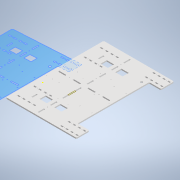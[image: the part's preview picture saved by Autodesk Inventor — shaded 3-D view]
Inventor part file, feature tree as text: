
AUTODESK INVENTOR PART (.ipt)
format: ipt  version: 2021.1 (Build 251245010, 245A)  size: 566,784 bytes
history: native  units: mm
features: reference x52, other x8, sketch x6, extrude x5
ambient origin geometry x8: Origin, YZ Plane, XZ Plane, XY Plane, X Axis, Y Axis, Z Axis, Center Point
bodies: Body1 (feature_tree)
feature tree (71):
  other  "РабПлоскость1"
  extrude  "Корпус"  Depth=6.2mm
  extrude  "Отверстия"  Depth=6.2mm
  extrude  "Выдавливание5"  TaperAngle=0.0deg  [1 undecoded]
  extrude  "Выдавливание6"  Depth=4.0mm
  sketch  "Эскиз8"
  extrude  "Выдавливание7"  Depth=6.2mm
  sketch  "Эскиз2"
  reference  "Ссылка16"
  reference  "Ссылка17"
  reference  "Ссылка18"
  reference  "Ссылка19"
  reference  "Ссылка20"
  reference  "Ссылка21"
  reference  "Ссылка22"
  reference  "Ссылка23"
  reference  "Ссылка24"
  reference  "Ссылка25"
  reference  "Ссылка26"
  reference  "Ссылка27"
  reference  "Ссылка28"
  reference  "Ссылка29"
  reference  "Ссылка30"
  reference  "Ссылка31"
  sketch  "Эскиз3"
  reference  "Ссылка32"
  reference  "Ссылка33"
  reference  "Ссылка34"
  reference  "Ссылка35"
  reference  "Ссылка36"
  reference  "Ссылка37"
  reference  "Ссылка38"
  reference  "Ссылка39"
  reference  "Ссылка40"
  reference  "Ссылка41"
  reference  "Ссылка42"
  reference  "Ссылка43"
  sketch  "Эскиз6"
  reference  "Ссылка52"
  reference  "Ссылка53"
  reference  "Ссылка54"
  sketch  "Эскиз7"
  reference  "Ссылка55"
  reference  "Ссылка57"
  reference  "Ссылка58"
  sketch  "Эскиз9"
  reference  "Ссылка59"
  reference  "Ссылка60"
  reference  "Ссылка61"
  reference  "Ссылка62"
  reference  "Ссылка63"
  reference  "Ссылка64"
  reference  "Ссылка65"
  reference  "Ссылка67"
  reference  "Ссылка68"
  reference  "Ссылка69"
  reference  "Ссылка70"
  reference  "Ссылка71"
  reference  "Ссылка72"
  reference  "Ссылка73"
  reference  "Ссылка74"
  reference  "Ссылка75"
  reference  "Ссылка76"
  reference  "Ссылка77"
  other  "<userpath>\Documents\Savka\3d\Korp.iam"
  other  "Korp.iam"
  other  "Korpus 2:1"
  other  "Korpus:1"
  other  "Korpus 5:1"
  other  "корпус:1"
  other  "Platforma_kolesa:1"
note: 1 required parameter value undecoded (feature->parameter linkage not recoverable at this tier; creation-order binding heuristic only, values carry confidence <= 0.55)
